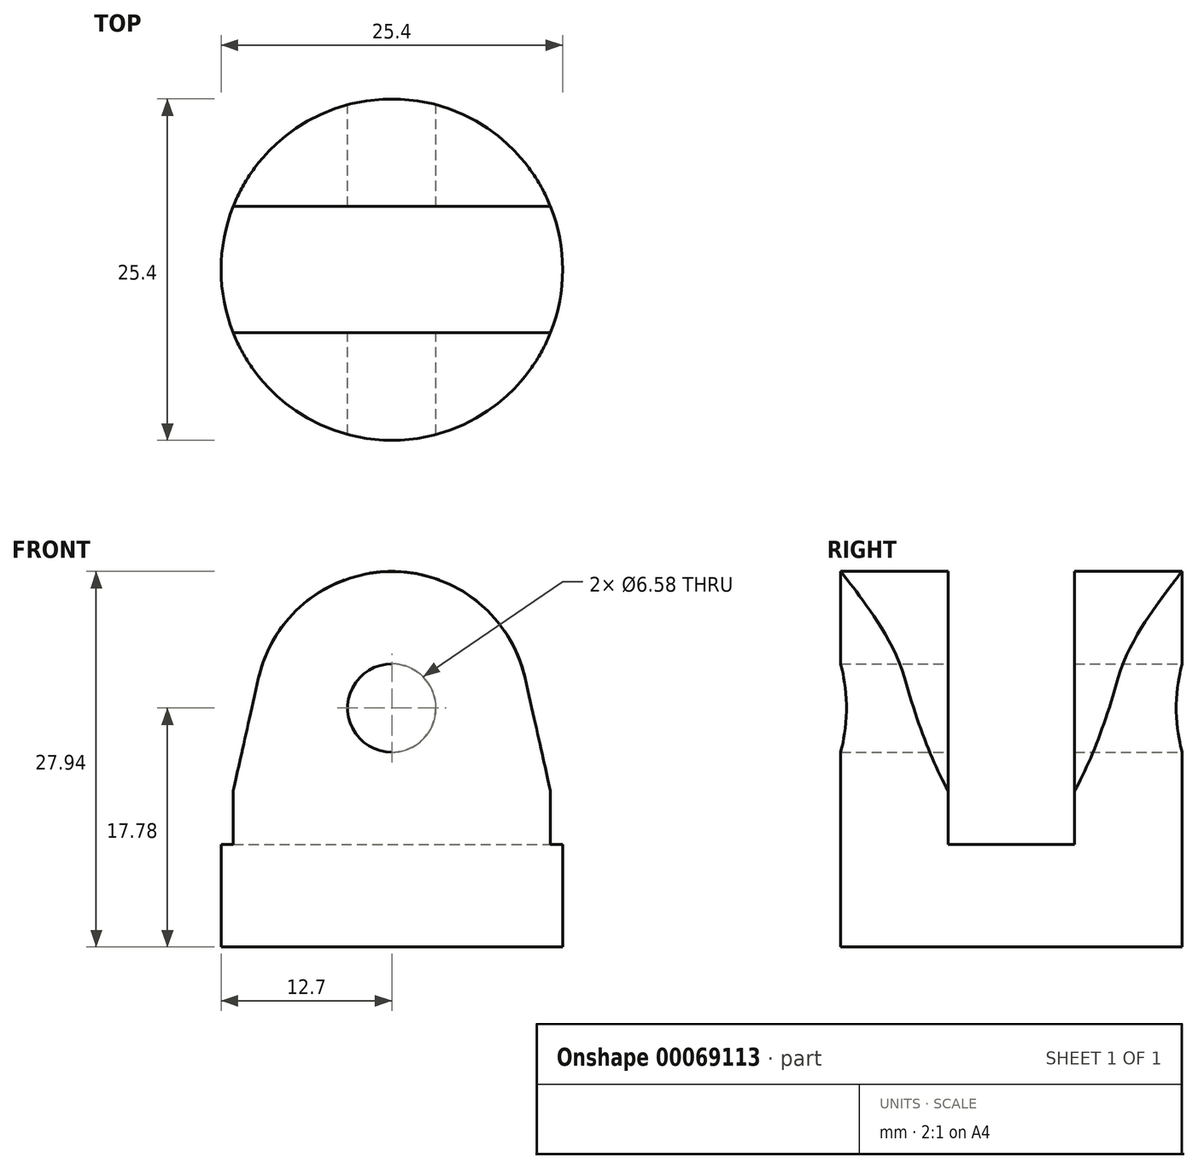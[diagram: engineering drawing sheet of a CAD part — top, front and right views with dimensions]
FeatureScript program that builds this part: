
annotation { "Feature Type Name" : "Feature", "Feature Type Description" : "" }
export const myFeature = defineFeature(function(context is Context, id is Id, definition is map)
    precondition{}
    {
        {
            var Q0;
            Q0=qCreatedBy(makeId("Top.planeOp"),FACE);
            var sketch = newSketch(context, id + "F0", { "sketchPlane" : qUnion([Q0])});
            skCircle(sketch, "E0", {"center": v(0, 0) * mm, "radius": 12.7 * mm});
            skSolve(sketch);
        }
        {
            var Q0;
            Q0=makeQuery(id+"F0.imprint","IMPRINT",FACE,{"disambiguationData":[TD([[makeQuery(id+"F0.imprint","IMPRINT",EDGE,{"derivedFrom":sQuery(id+"F0.wireOp",EDGE,"E0")}),1.0]])]});
            extrude(context, id + "F1", {"entities" : qUnion([Q0]), "depth" : 7.62 * mm});
        }
        {
            var Q0;
            Q0=qCreatedBy(makeId("Front.planeOp"),FACE);
            var sketch = newSketch(context, id + "F2", { "sketchPlane" : qUnion([Q0])});
            skCircle(sketch, "E1", {"center": v(0, 17.78) * mm, "radius": 10.16 * mm});
            skLineSegment(sketch, "E2", {"start": v(-9.91, 20.01) * mm, "end": v(-12.7, 7.62) * mm});
            skLineSegment(sketch, "E3", {"start": v(0, 7.62) * mm, "end": v(-12.7, 7.62) * mm});
            skLineSegment(sketch, "E4", {"start": v(0, 7.62) * mm, "end": v(0, 27.94) * mm});
            skCircle(sketch, "E5", {"center": v(0, 17.78) * mm, "radius": 3.29 * mm});
            skLineSegment(sketch, "E6.0.MirrorCS", {"start": v(9.91, 20.01) * mm, "end": v(12.7, 7.62) * mm});
            skLineSegment(sketch, "E7.0.MirrorCS", {"start": v(0, 7.62) * mm, "end": v(12.7, 7.62) * mm});
            skSolve(sketch);
        }
        {
            var Q0;
            {var subQ0=sQuery(id+"F2.wireOp",EDGE,"E5");var subQ1=sQuery(id+"F2.wireOp",EDGE,"E4");var subQ3=makeQuery(id+"F2.imprint","INTERSECT",VERTEX,{"disambiguationData":[OD(0.0)],"derivedFrom":[subQ1,subQ0]});Q0=makeQuery(id+"F2.imprint","IMPRINT",FACE,{"disambiguationData":[TD([[makeQuery(id+"F2.imprint","IMPRINT",EDGE,{"disambiguationData":[TD([[subQ3,-1.0]])],"derivedFrom":subQ1}),1.0]])]});}
            var Q1;
            {var subQ0=sQuery(id+"F2.wireOp",EDGE,"E5");var subQ1=sQuery(id+"F2.wireOp",EDGE,"E4");var subQ3=makeQuery(id+"F2.imprint","INTERSECT",VERTEX,{"disambiguationData":[OD(0.0)],"derivedFrom":[subQ1,subQ0]});Q1=makeQuery(id+"F2.imprint","IMPRINT",FACE,{"disambiguationData":[TD([[makeQuery(id+"F2.imprint","IMPRINT",EDGE,{"disambiguationData":[TD([[subQ3,-1.0]])],"derivedFrom":subQ1}),-1.0]])]});}
            extrude(context, id + "F3", {"entities" : qUnion([Q0, Q1]), "operationType" : NewBodyOperationType.REMOVE, "endBound" : BoundingType.SYMMETRIC, "oppositeDirection" : true, "depth" : 25.4 * mm});
        }
        {
            var Q0;
            Q0=qCreatedBy(makeId("Right.planeOp"),FACE);
            var sketch = newSketch(context, id + "F4", { "sketchPlane" : qUnion([Q0])});
            skLineSegment(sketch, "E8", {"start": v(0, 0) * mm, "end": v(0, 7.62) * mm});
            skLineSegment(sketch, "E9", {"start": v(0, 7.62) * mm, "end": v(-12.7, 7.62) * mm});
            skLineSegment(sketch, "E10", {"start": v(-12.7, 7.62) * mm, "end": v(12.7, 7.62) * mm});
            skLineSegment(sketch, "E11", {"start": v(-4.7, 7.62) * mm, "end": v(-4.7, 28.9) * mm});
            skLineSegment(sketch, "E12", {"start": v(-4.7, 28.9) * mm, "end": v(4.7, 28.9) * mm});
            skLineSegment(sketch, "E13", {"start": v(4.7, 28.9) * mm, "end": v(4.7, 7.62) * mm});
            skLineSegment(sketch, "E14", {"start": v(4.7, 28.9) * mm, "end": v(0, 28.9) * mm});
            skLineSegment(sketch, "E15", {"start": v(0, 28.9) * mm, "end": v(-4.7, 28.9) * mm});
            skLineSegment(sketch, "E16.bottom", {"start": v(4.7, 7.62) * mm, "end": v(9.6, 7.62) * mm});
            skLineSegment(sketch, "E16.top", {"start": v(4.7, 29.37) * mm, "end": v(9.6, 29.37) * mm});
            skLineSegment(sketch, "E16.left", {"start": v(4.7, 7.62) * mm, "end": v(4.7, 29.37) * mm});
            skLineSegment(sketch, "E16.right", {"start": v(9.6, 7.62) * mm, "end": v(9.6, 29.37) * mm});
            skLineSegment(sketch, "E17.bottom", {"start": v(-4.7, 7.62) * mm, "end": v(-9.6, 7.62) * mm});
            skLineSegment(sketch, "E17.top", {"start": v(-4.7, 27.94) * mm, "end": v(-9.6, 27.94) * mm});
            skLineSegment(sketch, "E17.left", {"start": v(-4.7, 7.62) * mm, "end": v(-4.7, 27.94) * mm});
            skLineSegment(sketch, "E17.right", {"start": v(-9.6, 7.62) * mm, "end": v(-9.6, 27.94) * mm});
            skLineSegment(sketch, "E18.bottom", {"start": v(-12.7, 7.62) * mm, "end": v(-9.6, 7.62) * mm});
            skLineSegment(sketch, "E18.top", {"start": v(-12.7, 27.94) * mm, "end": v(-9.6, 27.94) * mm});
            skLineSegment(sketch, "E18.left", {"start": v(-12.7, 7.62) * mm, "end": v(-12.7, 27.94) * mm});
            skLineSegment(sketch, "E19.bottom", {"start": v(12.7, 7.62) * mm, "end": v(9.6, 7.62) * mm});
            skLineSegment(sketch, "E19.top", {"start": v(12.7, 29.37) * mm, "end": v(9.6, 29.37) * mm});
            skLineSegment(sketch, "E19.left", {"start": v(12.7, 7.62) * mm, "end": v(12.7, 29.37) * mm});
            skSolve(sketch);
        }
        {
            var Q0;
            Q0=makeQuery(id+"F4.imprint","IMPRINT",FACE,{"disambiguationData":[TD([[makeQuery(id+"F4.imprint","IMPRINT",EDGE,{"derivedFrom":sQuery(id+"F4.wireOp",EDGE,"E19.bottom")}),-1.0]])]});
            var Q1;
            Q1=makeQuery(id+"F4.imprint","IMPRINT",FACE,{"disambiguationData":[TD([[makeQuery(id+"F4.imprint","IMPRINT",EDGE,{"derivedFrom":sQuery(id+"F4.wireOp",EDGE,"E11")}),-1.0]])]});
            var Q2;
            Q2=makeQuery(id+"F4.imprint","IMPRINT",FACE,{"disambiguationData":[TD([[makeQuery(id+"F4.imprint","IMPRINT",EDGE,{"derivedFrom":sQuery(id+"F4.wireOp",EDGE,"E18.bottom")}),1.0]])]});
            extrude(context, id + "F5", {"entities" : qUnion([Q0, Q1, Q2]), "operationType" : NewBodyOperationType.REMOVE, "endBound" : BoundingType.SYMMETRIC, "oppositeDirection" : true, "depth" : 25.4 * mm});
        }
        {
            var Q0;
            Q0=qSketchRegion(id+"F2",true);
            extrude(context, id + "F6", {"entities" : qUnion([Q0]), "operationType" : NewBodyOperationType.ADD, "endBound" : BoundingType.SYMMETRIC, "depth" : 25.4 * mm});
        }
        {
            var Q0;
            {var subQ0=sQuery(id+"F2.wireOp",EDGE,"E3");var subQ1=sQuery(id+"F2.wireOp",EDGE,"E7.0.MirrorCS");var subQ2=makeQuery(id+"F6.opExtrude","SWEPT_FACE",FACE,{"disambiguationData":[OSD([subQ0,subQ1])]});var subQ3=sQuery(id+"F2.wireOp",EDGE,"E2");Q0=makeQuery(id+"F6.boolean.opBoolean","SPLIT",FACE,{"disambiguationData":[TD([makeQuery(id+"F1.opExtrude","SWEPT_FACE",FACE,{"disambiguationData":[OSD([sQuery(id+"F0.wireOp",EDGE,"E0")])]}),makeQuery(id+"F6.opExtrude","CAP_FACE",FACE,{"disambiguationData":[OSD([sQuery(id+"F2.wireOp",EDGE,"E1"),subQ3,subQ0,sQuery(id+"F2.wireOp",EDGE,"E5"),sQuery(id+"F2.wireOp",EDGE,"E6.0.MirrorCS"),subQ1])],"isStart":true}),makeQuery(id+"F6.opExtrude","SWEPT_FACE",FACE,{"disambiguationData":[OSD([subQ3])]}),subQ2])],"derivedFrom":subQ2});}
            var Q1;
            {var subQ0=sQuery(id+"F2.wireOp",EDGE,"E3");var subQ1=sQuery(id+"F2.wireOp",EDGE,"E7.0.MirrorCS");var subQ2=makeQuery(id+"F6.opExtrude","SWEPT_FACE",FACE,{"disambiguationData":[OSD([subQ0,subQ1])]});var subQ3=sQuery(id+"F2.wireOp",EDGE,"E6.0.MirrorCS");Q1=makeQuery(id+"F6.boolean.opBoolean","SPLIT",FACE,{"disambiguationData":[TD([makeQuery(id+"F1.opExtrude","SWEPT_FACE",FACE,{"disambiguationData":[OSD([sQuery(id+"F0.wireOp",EDGE,"E0")])]}),makeQuery(id+"F6.opExtrude","CAP_FACE",FACE,{"disambiguationData":[OSD([sQuery(id+"F2.wireOp",EDGE,"E1"),sQuery(id+"F2.wireOp",EDGE,"E2"),subQ0,sQuery(id+"F2.wireOp",EDGE,"E5"),subQ3,subQ1])],"isStart":true}),subQ2,makeQuery(id+"F6.opExtrude","SWEPT_FACE",FACE,{"disambiguationData":[OSD([subQ3])]})])],"derivedFrom":subQ2});}
            var Q2;
            {var subQ0=sQuery(id+"F2.wireOp",EDGE,"E3");var subQ1=sQuery(id+"F2.wireOp",EDGE,"E7.0.MirrorCS");var subQ2=makeQuery(id+"F6.opExtrude","SWEPT_FACE",FACE,{"disambiguationData":[OSD([subQ0,subQ1])]});var subQ3=sQuery(id+"F2.wireOp",EDGE,"E6.0.MirrorCS");Q2=makeQuery(id+"F6.boolean.opBoolean","SPLIT",FACE,{"disambiguationData":[TD([makeQuery(id+"F1.opExtrude","SWEPT_FACE",FACE,{"disambiguationData":[OSD([sQuery(id+"F0.wireOp",EDGE,"E0")])]}),makeQuery(id+"F6.opExtrude","CAP_FACE",FACE,{"disambiguationData":[OSD([sQuery(id+"F2.wireOp",EDGE,"E1"),sQuery(id+"F2.wireOp",EDGE,"E2"),subQ0,sQuery(id+"F2.wireOp",EDGE,"E5"),subQ3,subQ1])],"isStart":false}),subQ2,makeQuery(id+"F6.opExtrude","SWEPT_FACE",FACE,{"disambiguationData":[OSD([subQ3])]})])],"derivedFrom":subQ2});}
            var Q3;
            {var subQ0=sQuery(id+"F2.wireOp",EDGE,"E3");var subQ1=sQuery(id+"F2.wireOp",EDGE,"E7.0.MirrorCS");var subQ2=makeQuery(id+"F6.opExtrude","SWEPT_FACE",FACE,{"disambiguationData":[OSD([subQ0,subQ1])]});var subQ3=sQuery(id+"F2.wireOp",EDGE,"E2");Q3=makeQuery(id+"F6.boolean.opBoolean","SPLIT",FACE,{"disambiguationData":[TD([makeQuery(id+"F1.opExtrude","SWEPT_FACE",FACE,{"disambiguationData":[OSD([sQuery(id+"F0.wireOp",EDGE,"E0")])]}),makeQuery(id+"F6.opExtrude","CAP_FACE",FACE,{"disambiguationData":[OSD([sQuery(id+"F2.wireOp",EDGE,"E1"),subQ3,subQ0,sQuery(id+"F2.wireOp",EDGE,"E5"),sQuery(id+"F2.wireOp",EDGE,"E6.0.MirrorCS"),subQ1])],"isStart":false}),makeQuery(id+"F6.opExtrude","SWEPT_FACE",FACE,{"disambiguationData":[OSD([subQ3])]}),subQ2])],"derivedFrom":subQ2});}
            extrude(context, id + "F7", {"entities" : qUnion([Q0, Q1, Q2, Q3]), "operationType" : NewBodyOperationType.REMOVE, "oppositeDirection" : true, "depth" : 25.4 * mm});
        }
        {
            var Q0;
            Q0=makeQuery(id+"F4.imprint","IMPRINT",FACE,{"disambiguationData":[TD([[makeQuery(id+"F4.imprint","IMPRINT",EDGE,{"derivedFrom":sQuery(id+"F4.wireOp",EDGE,"E19.bottom")}),-1.0]])]});
            var Q1;
            Q1=makeQuery(id+"F4.imprint","IMPRINT",FACE,{"disambiguationData":[TD([[makeQuery(id+"F4.imprint","IMPRINT",EDGE,{"derivedFrom":sQuery(id+"F4.wireOp",EDGE,"E11")}),-1.0]])]});
            var Q2;
            Q2=makeQuery(id+"F4.imprint","IMPRINT",FACE,{"disambiguationData":[TD([[makeQuery(id+"F4.imprint","IMPRINT",EDGE,{"derivedFrom":sQuery(id+"F4.wireOp",EDGE,"E18.bottom")}),1.0]])]});
            extrude(context, id + "F8", {"entities" : qUnion([Q0, Q1, Q2]), "operationType" : NewBodyOperationType.REMOVE, "endBound" : BoundingType.SYMMETRIC, "oppositeDirection" : true, "depth" : 25.4 * mm});
        }
    });
